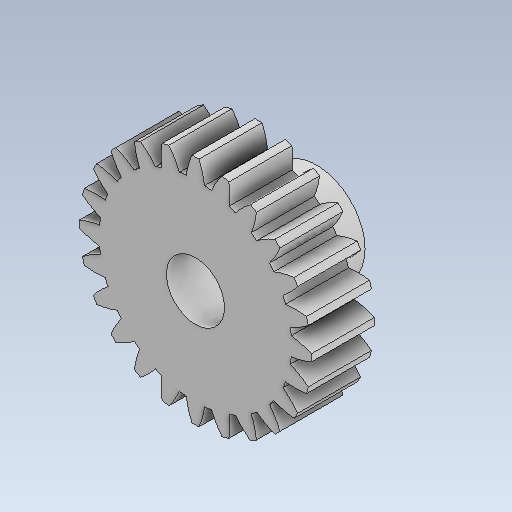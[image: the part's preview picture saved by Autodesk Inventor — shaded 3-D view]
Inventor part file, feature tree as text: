
AUTODESK INVENTOR PART (.ipt)
format: ipt  version: 2020 (Build 240168000, 168)  size: 318,464 bytes
history: native  units: mm
features: other x6, extrude x4, sketch x4, reference x4
ambient origin geometry x8: Origin, YZ Plane, XZ Plane, XY Plane, X Axis, Y Axis, Z Axis, Center Point
bodies: Body1 (feature_tree)
feature tree (18):
  other  "Bryła1"
  extrude  "Wyciągnięcie proste1"  Depth=7.6mm TaperAngle=0.0deg
  extrude  "Wyciągnięcie proste2"  Depth=5.7mm
  extrude  "Wyciągnięcie proste6"  Depth=4.0mm TaperAngle=0.0deg
  extrude  "Wyciągnięcie proste7"  Depth=3.0mm
  sketch  "Szkic1"
  reference  "Odniesienie1"
  sketch  "Szkic2"
  reference  "Odniesienie2"
  reference  "Odniesienie3"
  reference  "Odniesienie4"
  sketch  "Szkic6"
  sketch  "Szkic7"
  other  "<userpath>\Desktop\ScanBot\3d-model\Assembly1.iam"
  other  "Assembly1.iam"
  other  "wheel:1"
  other  "MG_996R:2"
  other  "Eje:1"
